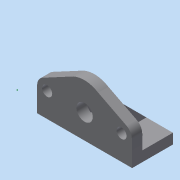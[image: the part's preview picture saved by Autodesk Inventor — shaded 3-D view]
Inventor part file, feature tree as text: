
AUTODESK INVENTOR PART (.ipt)
format: ipt  version: 2015 (Build 190159000, 159)  size: 265,728 bytes
history: native  units: in
note: dims shown in document units (in); Inventor stores cm internally (conversion verified against a paired STEP export)
features: sketch x16, extrude x13, hole x3, projected_geometry x2, mirror x1, fillet x1, chamfer x1
ambient origin geometry x8: Origin, YZ Plane, XZ Plane, XY Plane, X Axis, Y Axis, Z Axis, Center Point
bodies: Solid1 (feature_tree)
feature tree (37):
  extrude  "Extrusion1"  Depth=1.9685in
  sketch  "Sketch2"  dims[d2=0.7874in d3=0.0in d4=0.1969in]
  extrude  "Extrusion2"  Depth=0.1969in
  extrude  "Extrusion3"  Depth=0.1969in TaperAngle=0.0deg
  extrude  "Extrusion5"  Depth=0.1969in
  hole  "Hole1"  [1 undecoded]
  hole  "Hole2"  [1 undecoded]
  hole  "Hole3"  [1 undecoded]
  extrude  "Extrusion6"  Depth=0.5906in
  extrude  "Extrusion7"  Depth=0.5906in
  mirror  "Mirror1"
  sketch  "Sketch9"  dims[d30=0.5906in d31=0.4724in]
  fillet  "Fillet1"  Radius=0.3937in
  extrude  "Extrusion8"  Depth=0.3937in
  extrude  "Extrusion9"  Depth=0.1969in TaperAngle=0.0deg
  extrude  "Extrusion10"  TaperAngle=0.0deg  [1 undecoded]
  extrude  "Extrusion11"  Depth=0.344in
  chamfer  "Chamfer1"  Distance=0.5in
  extrude  "Extrusion12"  Depth=0.5906in
  extrude  "Extrusion13"  TaperAngle=0.0deg  [1 undecoded]
  extrude  "Extrusion14"  Depth=0.5906in TaperAngle=0.0deg
  sketch  "Sketch1"  dims[d0=1.9685in d1=1.9685in]
  sketch  "Sketch3"  dims[d5=0.1969in d6=0.2953in d7=0.0in]
  sketch  "Sketch4"  dims[d8=0.1969in d9=0.0in d12=0.5in]
  sketch  "Sketch5"  dims[d13=0.5in d14=0.0in d15=0.0in]
  sketch  "Sketch6"  dims[d17=0.2756in]
  sketch  "Sketch7"  dims[d20=0.315in d21=0.75in d22=0.375in d23=0.25in d24=0.5635in d25=1.0in d26=0.8108in d27=0.2756in]
  sketch  "Sketch8"  dims[d28=0.3937in d29=0.3937in]
  sketch  "Sketch10"  dims[d32=0.1969in d33=0.75in d34=0.375in d35=0.25in d36=0.5635in d37=1.0in d38=0.8108in d39=0.5906in d40=0.3937in]
  sketch  "Sketch12"  dims[d41=0.3937in d42=0.4724in]
  sketch  "Sketch13"  dims[d43=0.1969in d44=0.75in d45=0.375in d46=0.25in d47=0.5635in d48=1.0in d49=0.8108in d50=1.0in d51=0.0in]
  sketch  "Sketch14"  dims[d52=0.0in d53=0.0in d54=0.0in]
  sketch  "Sketch15"  dims[d55=0.315in d56=0.344in]
  projected_geometry  "Projected Loop1"
  sketch  "Sketch16"  dims[d57=0.333in]
  projected_geometry  "Projected Loop2"
  sketch  "Sketch17"  dims[d58=0.5in d59=0.5in d60=0.333in d61=0.0in d62=1.0in d63=0.0in d79=1.0in d80=0.0in d81=1.0in d82=0.0in d83=0.3937in d84=0.1969in d85=0.3937in d86=0.1969in d87=0.5906in d88=0.0in d89=0.5906in d90=0.0787in d91=45.0deg d92=0.1181in d93=0.0in d94=0.1181in d95=0.0in d96=0.0in d97=0.0in]
note: 5 required parameter values undecoded (feature->parameter linkage not recoverable at this tier; creation-order binding heuristic only, values carry confidence <= 0.55)
